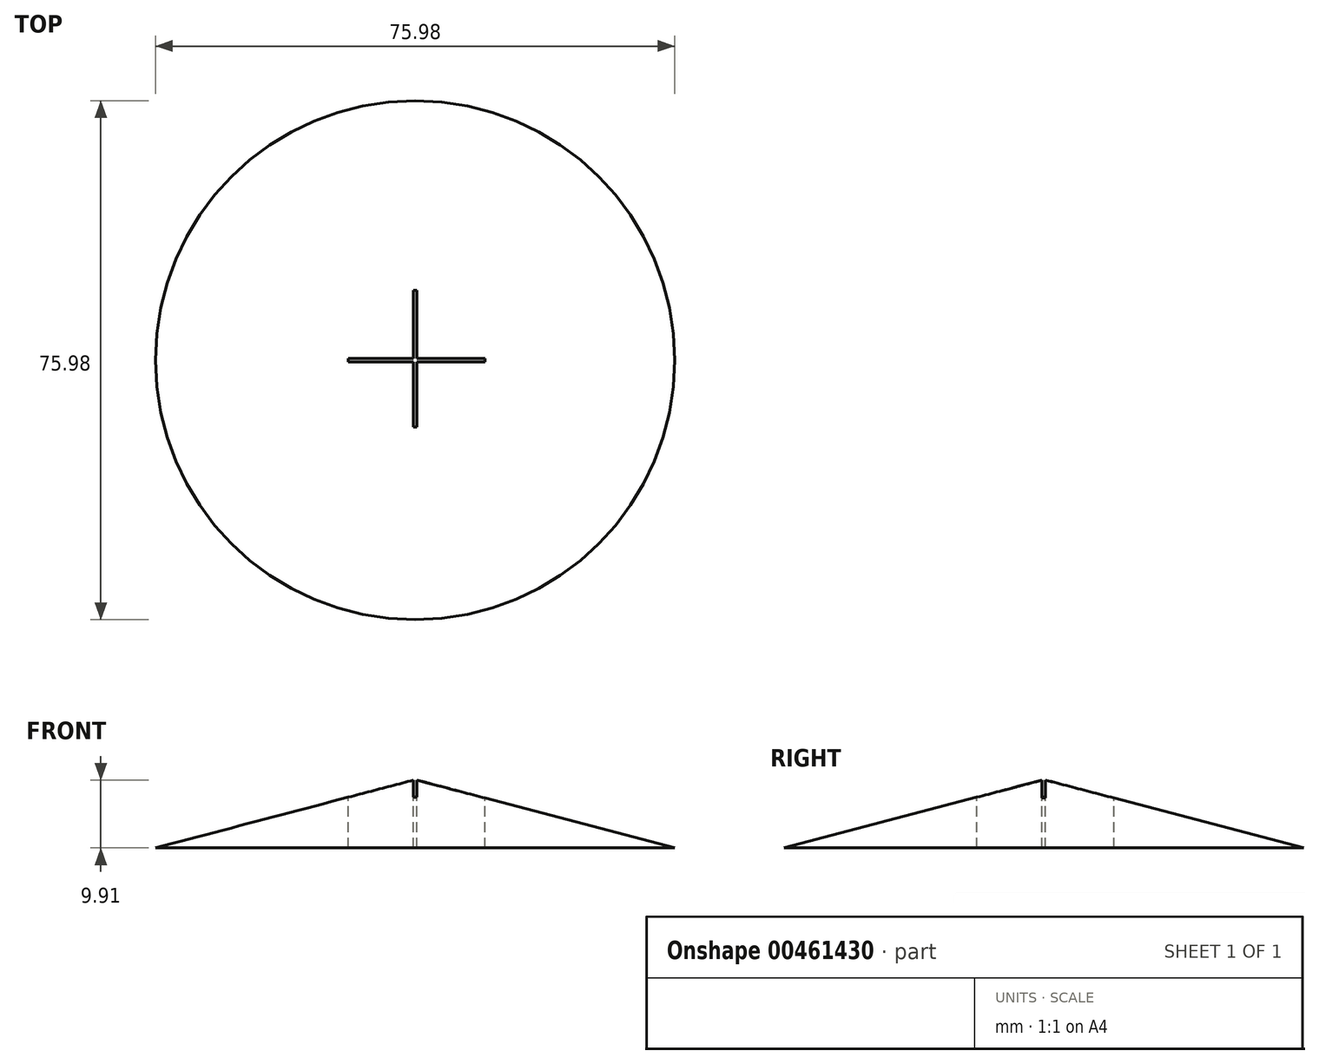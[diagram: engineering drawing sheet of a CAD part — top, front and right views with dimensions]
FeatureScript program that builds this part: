
annotation { "Feature Type Name" : "Feature", "Feature Type Description" : "" }
export const myFeature = defineFeature(function(context is Context, id is Id, definition is map)
    precondition{}
    {
        {
            var Q0;
            Q0=qCreatedBy(makeId("Top.planeOp"),FACE);
            var sketch = newSketch(context, id + "F0", { "sketchPlane" : qUnion([Q0])});
            skCircle(sketch, "E0", {"center": v(0, 0) * mm, "radius": 38 * mm});
            skSolve(sketch);
        }
        {
            var Q0;
            Q0=qCreatedBy(makeId("Front.planeOp"),FACE);
            var sketch = newSketch(context, id + "F1", { "sketchPlane" : qUnion([Q0])});
            skLineSegment(sketch, "E1", {"start": v(-38, 0) * mm, "end": v(0, 10) * mm});
            skLineSegment(sketch, "E2", {"start": v(0, 10) * mm, "end": v(0, 0) * mm});
            skLineSegment(sketch, "E3", {"start": v(0, 0) * mm, "end": v(-38, 0) * mm});
            skSolve(sketch);
        }
        {
            var Q0;
            Q0=makeQuery(id+"F1.imprint","IMPRINT",FACE,{"disambiguationData":[TD([[makeQuery(id+"F1.imprint","IMPRINT",EDGE,{"derivedFrom":sQuery(id+"F1.wireOp",EDGE,"E1")}),-1.0]])]});
            var Q1;
            Q1=sQuery(id+"F0.wireOp",EDGE,"E0");
            revolve(context, id + "F2", {"entities" : qUnion([Q0]), "axis" : qUnion([Q1]), "revolveType" : RevolveType.FULL});
        }
        {
            var Q0;
            Q0=qCreatedBy(makeId("Top.planeOp"),FACE);
            cPlane(context, id + "F3", {"entities" : qUnion([Q0]), "cplaneType" : CPlaneType.OFFSET, "offset" : 10.1 * mm, "width" : 150 * mm, "height" : 150 * mm});
        }
        {
            var Q0;
            Q0=qCreatedBy(id+"F3.planeOp",FACE);
            var sketch = newSketch(context, id + "F4", { "sketchPlane" : qUnion([Q0])});
            skLineSegment(sketch, "E4.bottom", {"start": v(-9.75, 0.23) * mm, "end": v(10.25, 0.23) * mm});
            skLineSegment(sketch, "E4.top", {"start": v(-9.75, -0.27) * mm, "end": v(10.25, -0.27) * mm});
            skLineSegment(sketch, "E4.left", {"start": v(-9.75, 0.23) * mm, "end": v(-9.75, -0.27) * mm});
            skLineSegment(sketch, "E4.right", {"start": v(10.25, 0.23) * mm, "end": v(10.25, -0.27) * mm});
            skLineSegment(sketch, "E5.bottom", {"start": v(-0.24, 10.22) * mm, "end": v(0.26, 10.22) * mm});
            skLineSegment(sketch, "E5.top", {"start": v(-0.24, -9.78) * mm, "end": v(0.26, -9.78) * mm});
            skLineSegment(sketch, "E5.left", {"start": v(-0.24, 10.22) * mm, "end": v(-0.24, -9.78) * mm});
            skLineSegment(sketch, "E5.right", {"start": v(0.26, 10.22) * mm, "end": v(0.26, -9.78) * mm});
            skSolve(sketch);
        }
        {
            var Q0;
            Q0 = qSketchRegion(id + "F4", true);
            extrude(context, id + "F5", {"entities" : qUnion([Q0]), "operationType" : NewBodyOperationType.REMOVE, "oppositeDirection" : true, "depth" : 25 * mm});
        }
    });
